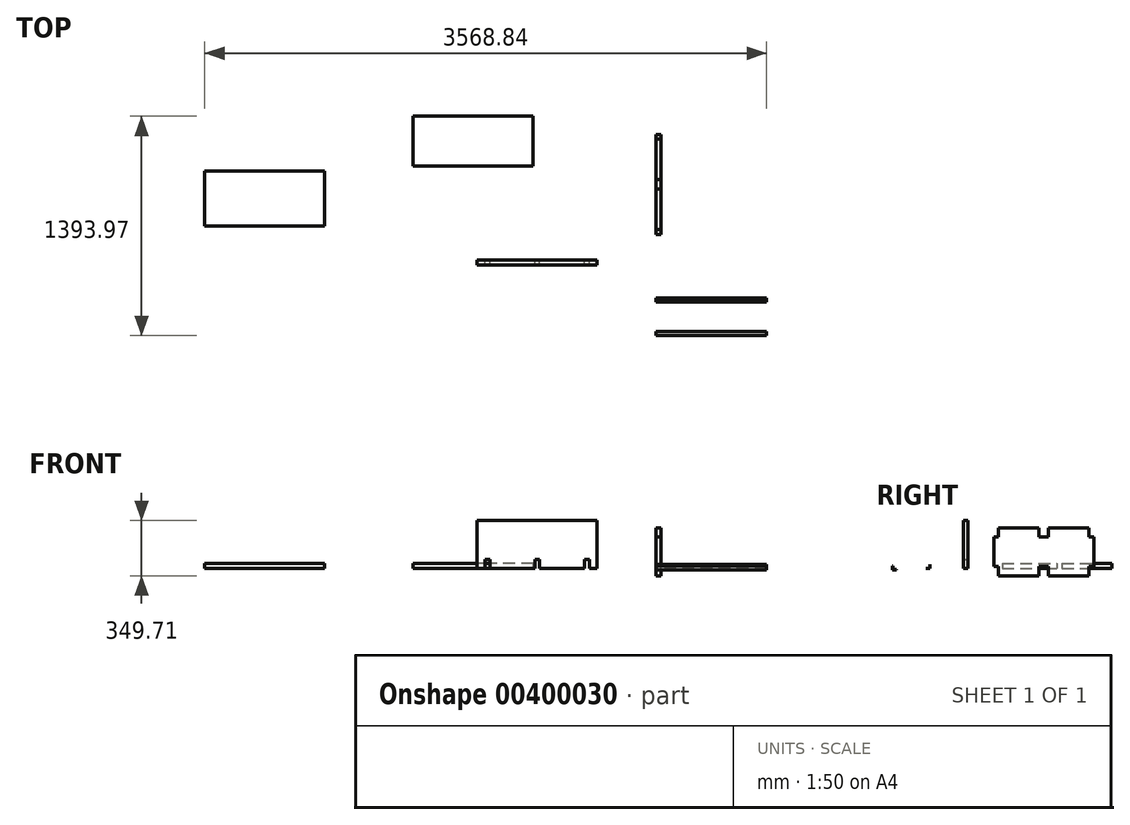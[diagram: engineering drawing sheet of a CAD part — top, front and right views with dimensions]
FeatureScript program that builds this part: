
annotation { "Feature Type Name" : "Feature", "Feature Type Description" : "" }
export const myFeature = defineFeature(function(context is Context, id is Id, definition is map)
    precondition{}
    {
        {
            var Q0;
            Q0=qCreatedBy(makeId("Right.planeOp"),FACE);
            var sketch = newSketch(context, id + "F0", { "sketchPlane" : qUnion([Q0])});
            skLineSegment(sketch, "E0.bottom", {"start": v(178.74, 257.61) * mm, "end": v(813.74, 257.61) * mm});
            skLineSegment(sketch, "E0.top", {"start": v(178.74, -47.19) * mm, "end": v(813.74, -47.19) * mm});
            skLineSegment(sketch, "E0.left", {"start": v(178.74, 257.61) * mm, "end": v(178.74, -47.19) * mm});
            skLineSegment(sketch, "E0.right", {"start": v(813.74, 257.61) * mm, "end": v(813.74, -47.19) * mm});
            skLineSegment(sketch, "E1.bottom", {"start": v(178.74, -47.19) * mm, "end": v(208.74, -47.19) * mm});
            skLineSegment(sketch, "E1.top", {"start": v(178.74, 12.81) * mm, "end": v(208.74, 12.81) * mm});
            skLineSegment(sketch, "E1.left", {"start": v(178.74, -47.19) * mm, "end": v(178.74, 12.81) * mm});
            skLineSegment(sketch, "E1.right", {"start": v(208.74, -47.19) * mm, "end": v(208.74, 12.81) * mm});
            skLineSegment(sketch, "E2.bottom", {"start": v(813.74, -47.19) * mm, "end": v(783.74, -47.19) * mm});
            skLineSegment(sketch, "E2.top", {"start": v(813.74, 12.81) * mm, "end": v(783.74, 12.81) * mm});
            skLineSegment(sketch, "E2.left", {"start": v(813.74, -47.19) * mm, "end": v(813.74, 12.81) * mm});
            skLineSegment(sketch, "E2.right", {"start": v(783.74, -47.19) * mm, "end": v(783.74, 12.81) * mm});
            skLineSegment(sketch, "E3.bottom", {"start": v(496.24, -47.19) * mm, "end": v(466.24, -47.19) * mm});
            skLineSegment(sketch, "E3.top", {"start": v(496.24, 12.81) * mm, "end": v(466.24, 12.81) * mm});
            skLineSegment(sketch, "E3.left", {"start": v(496.24, -47.19) * mm, "end": v(496.24, 12.81) * mm});
            skLineSegment(sketch, "E3.right", {"start": v(466.24, -47.19) * mm, "end": v(466.24, 12.81) * mm});
            skLineSegment(sketch, "E4.bottom", {"start": v(496.24, 12.81) * mm, "end": v(526.24, 12.81) * mm});
            skLineSegment(sketch, "E4.top", {"start": v(496.24, -47.19) * mm, "end": v(526.24, -47.19) * mm});
            skLineSegment(sketch, "E4.left", {"start": v(496.24, 12.81) * mm, "end": v(496.24, -47.19) * mm});
            skLineSegment(sketch, "E4.right", {"start": v(526.24, 12.81) * mm, "end": v(526.24, -47.19) * mm});
            skLineSegment(sketch, "E5.bottom", {"start": v(813.74, 257.61) * mm, "end": v(783.74, 257.61) * mm});
            skLineSegment(sketch, "E5.top", {"start": v(813.74, 197.61) * mm, "end": v(783.74, 197.61) * mm});
            skLineSegment(sketch, "E5.left", {"start": v(813.74, 257.61) * mm, "end": v(813.74, 197.61) * mm});
            skLineSegment(sketch, "E5.right", {"start": v(783.74, 257.61) * mm, "end": v(783.74, 197.61) * mm});
            skLineSegment(sketch, "E6.bottom", {"start": v(178.74, 257.61) * mm, "end": v(208.74, 257.61) * mm});
            skLineSegment(sketch, "E6.top", {"start": v(178.74, 197.61) * mm, "end": v(208.74, 197.61) * mm});
            skLineSegment(sketch, "E6.left", {"start": v(178.74, 257.61) * mm, "end": v(178.74, 197.61) * mm});
            skLineSegment(sketch, "E6.right", {"start": v(208.74, 257.61) * mm, "end": v(208.74, 197.61) * mm});
            skLineSegment(sketch, "E7.bottom", {"start": v(526.24, 257.61) * mm, "end": v(496.24, 257.61) * mm});
            skLineSegment(sketch, "E7.top", {"start": v(526.24, 197.61) * mm, "end": v(496.24, 197.61) * mm});
            skLineSegment(sketch, "E7.left", {"start": v(496.24, 257.61) * mm, "end": v(496.24, 197.61) * mm});
            skLineSegment(sketch, "E7.right", {"start": v(526.24, 257.61) * mm, "end": v(526.24, 197.61) * mm});
            skLineSegment(sketch, "E8.bottom", {"start": v(466.24, 257.61) * mm, "end": v(496.24, 257.61) * mm});
            skLineSegment(sketch, "E8.top", {"start": v(466.24, 197.61) * mm, "end": v(496.24, 197.61) * mm});
            skLineSegment(sketch, "E8.right", {"start": v(466.24, 257.61) * mm, "end": v(466.24, 197.61) * mm});
            skSolve(sketch);
        }
        {
            var Q0;
            Q0=makeQuery(id+"F0.imprint","IMPRINT",FACE,{"disambiguationData":[TD([[makeQuery(id+"F0.imprint","IMPRINT",EDGE,{"derivedFrom":sQuery(id+"F0.wireOp",EDGE,"E0.bottom")}),-1.0]])]});
            extrude(context, id + "F1", {"entities" : qUnion([Q0]), "depth" : 30 * mm});
        }
        {
            var Q0;
            Q0=qCreatedBy(makeId("Front.planeOp"),FACE);
            var sketch = newSketch(context, id + "F2", { "sketchPlane" : qUnion([Q0])});
            skLineSegment(sketch, "E9.bottom", {"start": v(-373.94, -2.28) * mm, "end": v(-1135.94, -2.28) * mm});
            skLineSegment(sketch, "E9.top", {"start": v(-373.94, 302.52) * mm, "end": v(-1135.94, 302.52) * mm});
            skLineSegment(sketch, "E9.left", {"start": v(-373.94, -2.28) * mm, "end": v(-373.94, 302.52) * mm});
            skLineSegment(sketch, "E9.right", {"start": v(-1135.94, -2.28) * mm, "end": v(-1135.94, 302.52) * mm});
            skPoint(sketch, "E9.middle", {"position": v(-754.94, 150.12) * mm});
            skLineSegment(sketch, "E10.bottom", {"start": v(-1085.94, -2.28) * mm, "end": v(-1055.94, -2.28) * mm});
            skLineSegment(sketch, "E10.top", {"start": v(-1085.94, 57.72) * mm, "end": v(-1055.94, 57.72) * mm});
            skLineSegment(sketch, "E10.left", {"start": v(-1085.94, -2.28) * mm, "end": v(-1085.94, 57.72) * mm});
            skLineSegment(sketch, "E10.right", {"start": v(-1055.94, -2.28) * mm, "end": v(-1055.94, 57.72) * mm});
            skLineSegment(sketch, "E11.bottom", {"start": v(-423.94, -2.28) * mm, "end": v(-453.94, -2.28) * mm});
            skLineSegment(sketch, "E11.top", {"start": v(-423.94, 57.72) * mm, "end": v(-453.94, 57.72) * mm});
            skLineSegment(sketch, "E11.left", {"start": v(-423.94, -2.28) * mm, "end": v(-423.94, 57.72) * mm});
            skLineSegment(sketch, "E11.right", {"start": v(-453.94, -2.28) * mm, "end": v(-453.94, 57.72) * mm});
            skPoint(sketch, "E12.oppositeSnap0", {"position": v(-754.94, -2.28) * mm});
            skLineSegment(sketch, "E13.bottom", {"start": v(-769.94, -2.28) * mm, "end": v(-739.94, -2.28) * mm});
            skLineSegment(sketch, "E13.top", {"start": v(-769.94, 57.72) * mm, "end": v(-739.94, 57.72) * mm});
            skLineSegment(sketch, "E13.left", {"start": v(-769.94, -2.28) * mm, "end": v(-769.94, 57.72) * mm});
            skLineSegment(sketch, "E13.right", {"start": v(-739.94, -2.28) * mm, "end": v(-739.94, 57.72) * mm});
            skLineSegment(sketch, "E14.bottom", {"start": v(-769.94, 302.52) * mm, "end": v(-739.94, 302.52) * mm});
            skSolve(sketch);
        }
        {
            var Q0;
            Q0=makeQuery(id+"F2.imprint","IMPRINT",FACE,{"disambiguationData":[TD([[makeQuery(id+"F2.imprint","IMPRINT",EDGE,{"derivedFrom":sQuery(id+"F2.wireOp",EDGE,"E9.top")}),1.0]])]});
            extrude(context, id + "F3", {"entities" : qUnion([Q0]), "endBound" : BoundingType.SYMMETRIC, "depth" : 30 * mm});
        }
        {
            var Q0;
            Q0=qCreatedBy(makeId("Top.planeOp"),FACE);
            var sketch = newSketch(context, id + "F4", { "sketchPlane" : qUnion([Q0])});
            skLineSegment(sketch, "E15.bottom", {"start": v(-780.6, 612.32) * mm, "end": v(-1542.6, 612.32) * mm});
            skLineSegment(sketch, "E15.top", {"start": v(-780.6, 929.82) * mm, "end": v(-1542.6, 929.82) * mm});
            skLineSegment(sketch, "E15.left", {"start": v(-780.6, 612.32) * mm, "end": v(-780.6, 929.82) * mm});
            skLineSegment(sketch, "E15.right", {"start": v(-1542.6, 612.32) * mm, "end": v(-1542.6, 929.82) * mm});
            skPoint(sketch, "E15.middle", {"position": v(-1161.6, 771.07) * mm});
            skSolve(sketch);
        }
        {
            var Q0;
            Q0=makeQuery(id+"F4.imprint","IMPRINT",FACE,{"disambiguationData":[TD([[makeQuery(id+"F4.imprint","IMPRINT",EDGE,{"derivedFrom":sQuery(id+"F4.wireOp",EDGE,"E15.bottom")}),-1.0]])]});
            extrude(context, id + "F5", {"entities" : qUnion([Q0]), "depth" : 30 * mm});
        }
        {
            var Q0;
            Q0=qCreatedBy(makeId("Top.planeOp"),FACE);
            var sketch = newSketch(context, id + "F6", { "sketchPlane" : qUnion([Q0])});
            skLineSegment(sketch, "E16.bottom", {"start": v(-2104.84, 232.4) * mm, "end": v(-2866.84, 232.4) * mm});
            skLineSegment(sketch, "E16.top", {"start": v(-2104.84, 579.9) * mm, "end": v(-2866.84, 579.9) * mm});
            skLineSegment(sketch, "E16.left", {"start": v(-2104.84, 232.4) * mm, "end": v(-2104.84, 579.9) * mm});
            skLineSegment(sketch, "E16.right", {"start": v(-2866.84, 232.4) * mm, "end": v(-2866.84, 579.9) * mm});
            skPoint(sketch, "E16.middle", {"position": v(-2485.84, 406.15) * mm});
            skSolve(sketch);
        }
        {
            var Q0;
            Q0=makeQuery(id+"F6.imprint","IMPRINT",FACE,{"disambiguationData":[TD([[makeQuery(id+"F6.imprint","IMPRINT",EDGE,{"derivedFrom":sQuery(id+"F6.wireOp",EDGE,"E16.bottom")}),-1.0]])]});
            extrude(context, id + "F7", {"entities" : qUnion([Q0]), "depth" : 30 * mm});
        }
        {
            var Q0;
            Q0=qCreatedBy(makeId("Right.planeOp"),FACE);
            var sketch = newSketch(context, id + "F8", { "sketchPlane" : qUnion([Q0])});
            skLineSegment(sketch, "E17", {"start": v(-464.15, 14.74) * mm, "end": v(-464.15, -10.66) * mm});
            skLineSegment(sketch, "E18", {"start": v(-464.15, -10.66) * mm, "end": v(-438.75, -10.66) * mm});
            skLineSegment(sketch, "E19", {"start": v(-438.75, -10.66) * mm, "end": v(-438.75, -8.66) * mm});
            skLineSegment(sketch, "E20", {"start": v(-438.75, -8.66) * mm, "end": v(-462.15, -8.66) * mm});
            skLineSegment(sketch, "E21", {"start": v(-462.15, -8.66) * mm, "end": v(-462.15, 14.74) * mm});
            skLineSegment(sketch, "E22", {"start": v(-462.15, 14.74) * mm, "end": v(-464.15, 14.74) * mm});
            skSolve(sketch);
        }
        {
            var Q0;
            Q0=makeQuery(id+"F8.imprint","IMPRINT",FACE,{"disambiguationData":[TD([[makeQuery(id+"F8.imprint","IMPRINT",EDGE,{"derivedFrom":sQuery(id+"F8.wireOp",EDGE,"E17")}),1.0]])]});
            extrude(context, id + "F9", {"entities" : qUnion([Q0]), "depth" : 762 * mm - 60 * mm});
        }
        {
            var Q0;
            Q0=qCreatedBy(makeId("Right.planeOp"),FACE);
            var sketch = newSketch(context, id + "F10", { "sketchPlane" : qUnion([Q0])});
            skLineSegment(sketch, "E23", {"start": v(-225.68, 23.4) * mm, "end": v(-225.68, -2) * mm});
            skLineSegment(sketch, "E24", {"start": v(-225.68, -2) * mm, "end": v(-251.08, -2) * mm});
            skLineSegment(sketch, "E25", {"start": v(-251.08, -2) * mm, "end": v(-251.08, 0) * mm});
            skLineSegment(sketch, "E26", {"start": v(-251.08, 0) * mm, "end": v(-227.68, 0) * mm});
            skLineSegment(sketch, "E27", {"start": v(-227.68, 0) * mm, "end": v(-227.68, 23.4) * mm});
            skLineSegment(sketch, "E28", {"start": v(-227.68, 23.4) * mm, "end": v(-225.68, 23.4) * mm});
            skSolve(sketch);
        }
        {
            var Q0;
            Q0=makeQuery(id+"F10.imprint","IMPRINT",FACE,{"disambiguationData":[TD([[makeQuery(id+"F10.imprint","IMPRINT",EDGE,{"derivedFrom":sQuery(id+"F10.wireOp",EDGE,"E23")}),-1.0]])]});
            extrude(context, id + "F11", {"entities" : qUnion([Q0]), "depth" : 762 * mm - 60 * mm});
        }
    });
